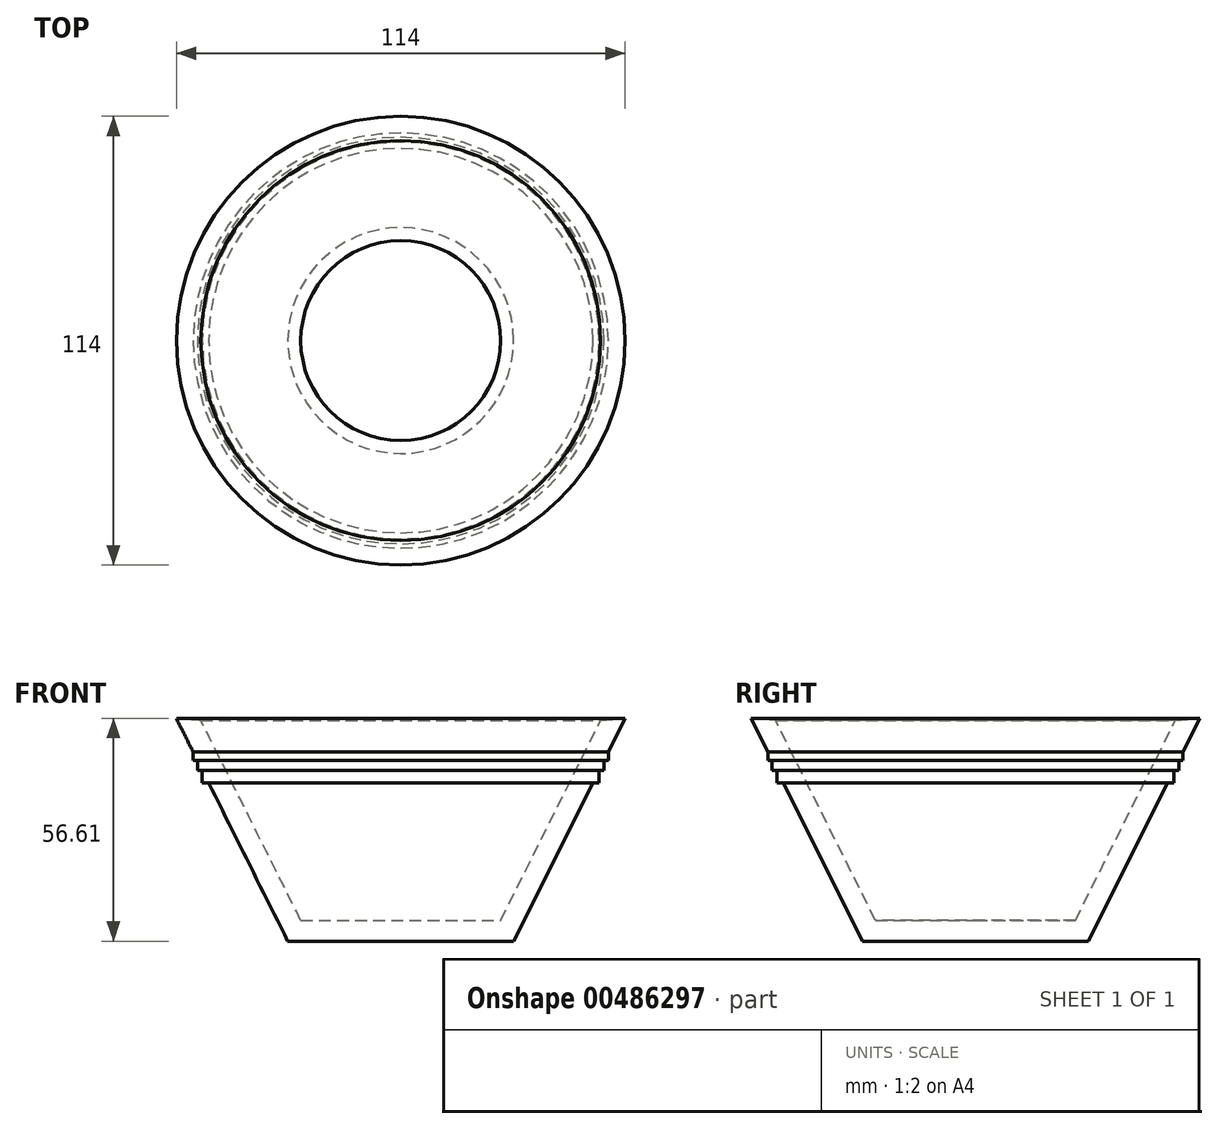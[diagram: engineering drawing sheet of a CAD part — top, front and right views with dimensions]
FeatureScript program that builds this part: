
annotation { "Feature Type Name" : "Feature", "Feature Type Description" : "" }
export const myFeature = defineFeature(function(context is Context, id is Id, definition is map)
    precondition{}
    {
        {
            var Q0;
            Q0=qCreatedBy(makeId("Front.planeOp"),FACE);
            var sketch = newSketch(context, id + "F0", { "sketchPlane" : qUnion([Q0])});
            skLineSegment(sketch, "E0", {"start": v(0, 0) * mm, "end": v(0, 50.8) * mm, "construction": true});
            skLineSegment(sketch, "E1", {"start": v(0, 0) * mm, "end": v(25.4, 0) * mm});
            skLineSegment(sketch, "E2", {"start": v(25.4, 0) * mm, "end": v(50.8, 50.8) * mm});
            skLineSegment(sketch, "E3.0", {"start": v(28.7, -5.33) * mm, "end": v(57, 51.28) * mm});
            skLineSegment(sketch, "E3.1", {"start": v(0, -5.33) * mm, "end": v(28.7, -5.33) * mm});
            skLineSegment(sketch, "E4", {"start": v(0, -5.33) * mm, "end": v(0, 0) * mm});
            skLineSegment(sketch, "E5", {"start": v(57, 51.28) * mm, "end": v(50.8, 50.8) * mm});
            skLineSegment(sketch, "E6", {"start": v(52.74, 42.75) * mm, "end": v(52.74, 40.56) * mm});
            skLineSegment(sketch, "E7", {"start": v(52.74, 40.56) * mm, "end": v(51.65, 40.56) * mm});
            skLineSegment(sketch, "E8", {"start": v(51.65, 40.56) * mm, "end": v(51.65, 38.1) * mm});
            skLineSegment(sketch, "E9", {"start": v(51.65, 38.1) * mm, "end": v(50.42, 38.1) * mm});
            skLineSegment(sketch, "E10", {"start": v(50.42, 38.1) * mm, "end": v(50.42, 34.93) * mm});
            skLineSegment(sketch, "E11", {"start": v(50.42, 34.93) * mm, "end": v(48.83, 34.93) * mm});
            skSolve(sketch);
        }
        {
            var Q0;
            Q0 = qSketchRegion(id + "F0", true);
            var Q1;
            Q1=sQuery(id+"F0.wireOp",EDGE,"E0");
            revolve(context, id + "F1", {"entities" : qUnion([Q0]), "axis" : qUnion([Q1]), "revolveType" : RevolveType.FULL});
        }
    });
